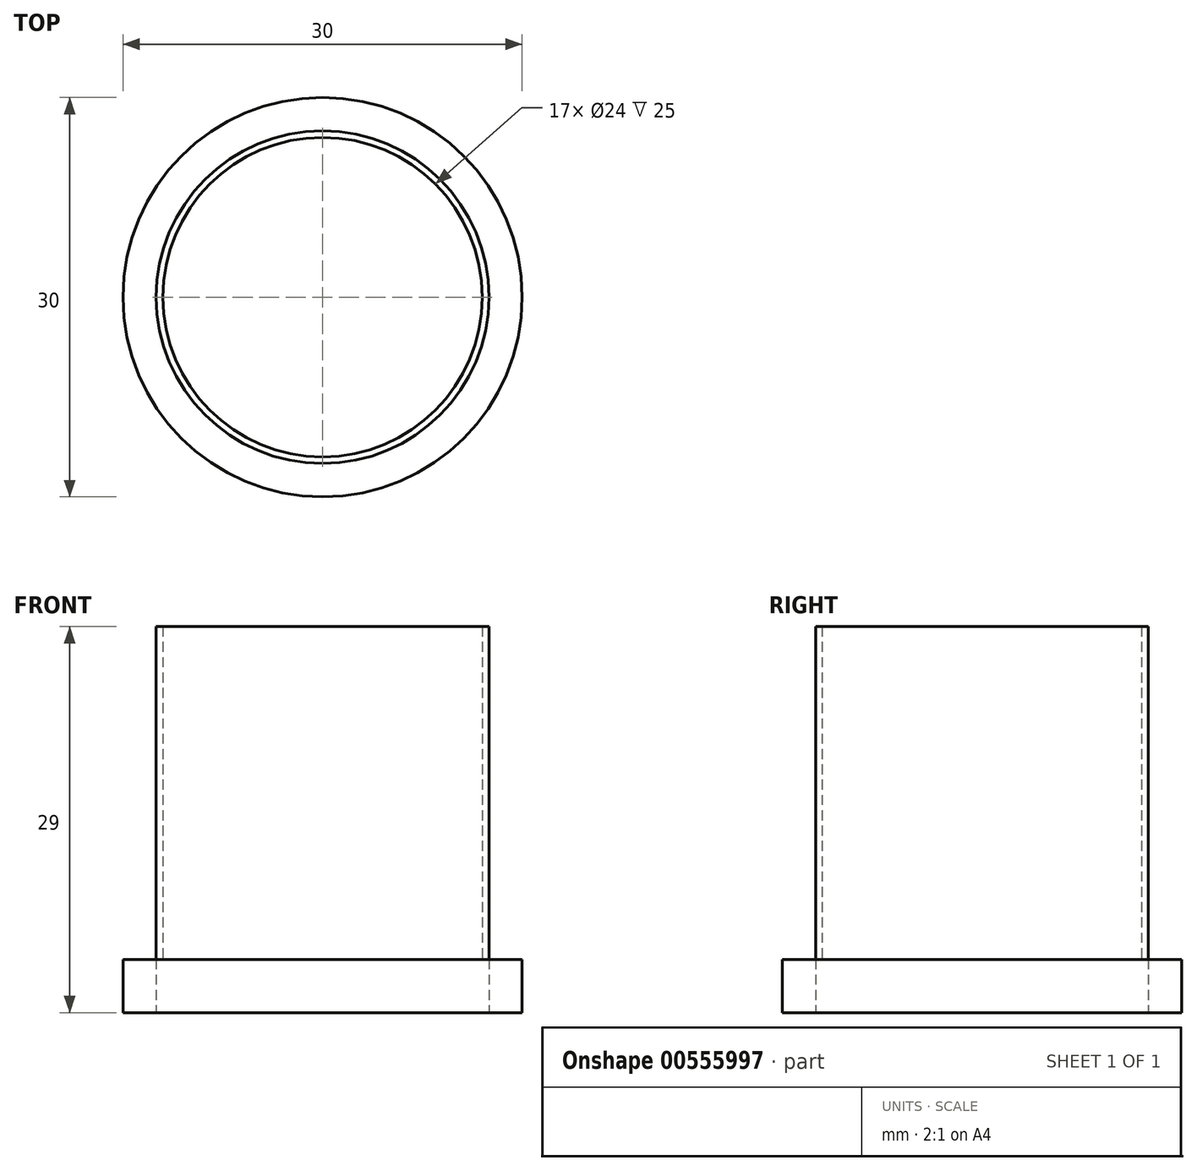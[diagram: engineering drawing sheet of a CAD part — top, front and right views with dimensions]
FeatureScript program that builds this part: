
annotation { "Feature Type Name" : "Feature", "Feature Type Description" : "" }
export const myFeature = defineFeature(function(context is Context, id is Id, definition is map)
    precondition{}
    {
        {
            var Q0;
            Q0=qCreatedBy(makeId("Top.planeOp"),FACE);
            var sketch = newSketch(context, id + "F0", { "sketchPlane" : qUnion([Q0])});
            skCircle(sketch, "E0", {"center": v(0, 0) * mm, "radius": 12.5 * mm});
            skCircle(sketch, "E1", {"center": v(0, 0) * mm, "radius": 15 * mm});
            skCircle(sketch, "E2", {"center": v(0, 0) * mm, "radius": 12.3 * mm});
            skSolve(sketch);
        }
        {
            var Q0;
            Q0=makeQuery(id+"F0.imprint","IMPRINT",FACE,{"disambiguationData":[TD([[makeQuery(id+"F0.imprint","IMPRINT",EDGE,{"derivedFrom":sQuery(id+"F0.wireOp",EDGE,"E0")}),-1.0]])]});
            var Q1;
            Q1=sQuery(id+"F0.wireOp",EDGE,"E0");
            var Q2;
            Q2=sQuery(id+"F0.wireOp",EDGE,"E1");
            extrude(context, id + "F1", {"entities" : qUnion([Q0]), "surfaceEntities" : qUnion([Q1, Q2]), "depth" : 4 * mm, "offsetDistance" : 25 * mm});
        }
        {
            var Q0;
            Q0=makeQuery(id+"F1.opExtrude","CAP_FACE",FACE,{"disambiguationData":[OSD([sQuery(id+"F0.wireOp",EDGE,"E0"),sQuery(id+"F0.wireOp",EDGE,"E1")])],"isStart":false});
            var sketch = newSketch(context, id + "F2", { "sketchPlane" : qUnion([Q0])});
            skCircle(sketch, "E3", {"center": v(0, 0) * mm, "radius": 12 * mm});
            skCircle(sketch, "E4", {"center": v(0, 0) * mm, "radius": 12.5 * mm});
            skSolve(sketch);
        }
        {
            var Q0;
            Q0 = qSketchRegion(id + "F2", true);
            extrude(context, id + "F3", {"entities" : qUnion([Q0]), "depth" : 25 * mm, "offsetDistance" : 25 * mm});
        }
    });
